# Revit family: Countertop_Stainless-Steel_Moduline
name_source: partatom
category: Furniture
units: mm (PartAtom-declared; Revit-internal decimal feet)

## family parameters
Always vertical = Yes
Classification Number = 23.40.20.00
Cut with Voids When Loaded = No
Enable Cutting in Views = No
Render Appearance Source = Family Geometry
Room Calculation Point = No
Shared = No
Work Plane-Based = No

## types (2) — shared parameters
Front Flange Height = 1.25 "
Height = 3.725 "
Keynote = 12 35 00
Manufacturer = Moduline Aluminum Cabinets
Model = Pro II Countertop
Product Page URL = https://www.arcat.com
Thickness = 0.079 "
URL = https://modulinecabinets.com
zero-valued in all types: Default Elevation

## per-type parameters (varying)
| type | Depth | Description | Sink Length |
| 24" Deep Stainless Steel | 24 " | Modular Countertop Stainless Steel , 24" Deep, .075" Thick, 1.25" Front Flange | 20 " |
| 18" Deep Stainless Steel | 18 " | Modular Countertop Stainless Steel , 18" Deep, .075" Thick, 1.25" Front Flange | 15 " |

## geometry (parser evidence)
native form markers: Sweep x2
no freeform markers — native parametric forms only
